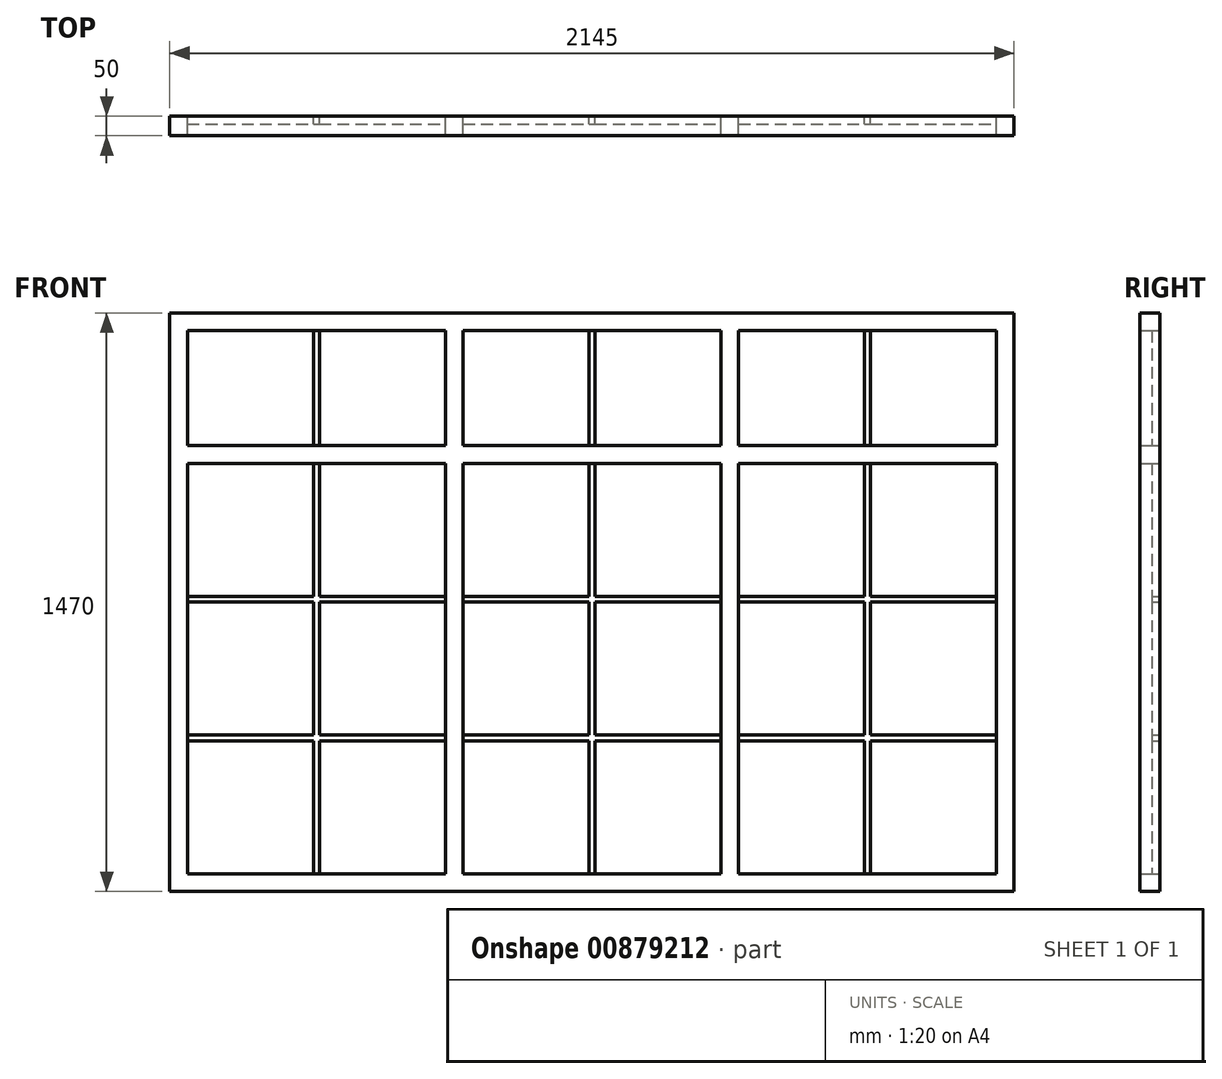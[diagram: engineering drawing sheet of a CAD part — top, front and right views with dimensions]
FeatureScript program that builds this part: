
annotation { "Feature Type Name" : "Feature", "Feature Type Description" : "" }
export const myFeature = defineFeature(function(context is Context, id is Id, definition is map)
    precondition{}
    {
        {
            var Q0;
            Q0=qCreatedBy(makeId("Front.planeOp"),FACE);
            var sketch = newSketch(context, id + "F0", { "sketchPlane" : qUnion([Q0])});
            skLineSegment(sketch, "E0.bottom", {"start": v(0, 0) * mm, "end": v(2145, 0) * mm});
            skLineSegment(sketch, "E0.top", {"start": v(0, 1470) * mm, "end": v(2145, 1470) * mm});
            skLineSegment(sketch, "E0.left", {"start": v(0, 0) * mm, "end": v(0, 1470) * mm});
            skLineSegment(sketch, "E0.right", {"start": v(2145, 0) * mm, "end": v(2145, 1470) * mm});
            skLineSegment(sketch, "E1.bottom", {"start": v(45, 1425) * mm, "end": v(700, 1425) * mm});
            skLineSegment(sketch, "E1.top", {"start": v(45, 45) * mm, "end": v(700, 45) * mm});
            skLineSegment(sketch, "E1.left", {"start": v(45, 1425) * mm, "end": v(45, 1132.5) * mm});
            skLineSegment(sketch, "E1.right", {"start": v(700, 1425) * mm, "end": v(700, 1132.5) * mm});
            skLineSegment(sketch, "E2.bottom", {"start": v(745, 1425) * mm, "end": v(1400, 1425) * mm});
            skLineSegment(sketch, "E2.top", {"start": v(745, 1132.5) * mm, "end": v(1400, 1132.5) * mm});
            skLineSegment(sketch, "E2.left", {"start": v(745, 1425) * mm, "end": v(745, 1132.5) * mm});
            skLineSegment(sketch, "E2.right", {"start": v(1400, 1425) * mm, "end": v(1400, 1132.5) * mm});
            skLineSegment(sketch, "E3.bottom", {"start": v(745, 1087.5) * mm, "end": v(1400, 1087.5) * mm});
            skLineSegment(sketch, "E3.top", {"start": v(745, 45) * mm, "end": v(1400, 45) * mm});
            skLineSegment(sketch, "E3.left", {"start": v(745, 1087.5) * mm, "end": v(745, 45) * mm});
            skLineSegment(sketch, "E3.right", {"start": v(1400, 1087.5) * mm, "end": v(1400, 45) * mm});
            skLineSegment(sketch, "E4.bottom", {"start": v(1445, 1425) * mm, "end": v(2100, 1425) * mm});
            skLineSegment(sketch, "E4.top", {"start": v(1445, 45) * mm, "end": v(2100, 45) * mm});
            skLineSegment(sketch, "E4.left", {"start": v(1445, 1425) * mm, "end": v(1445, 1132.5) * mm});
            skLineSegment(sketch, "E4.right", {"start": v(2100, 1425) * mm, "end": v(2100, 1132.5) * mm});
            skLineSegment(sketch, "E5.bottom", {"start": v(45, 1132.5) * mm, "end": v(700, 1132.5) * mm});
            skLineSegment(sketch, "E5.top", {"start": v(45, 1087.5) * mm, "end": v(700, 1087.5) * mm});
            skLineSegment(sketch, "E6.trimOffspring", {"start": v(45, 1087.5) * mm, "end": v(45, 45) * mm});
            skLineSegment(sketch, "E7.trimOffspring", {"start": v(700, 1087.5) * mm, "end": v(700, 45) * mm});
            skLineSegment(sketch, "E8.bottom", {"start": v(1445, 1132.5) * mm, "end": v(2100, 1132.5) * mm});
            skLineSegment(sketch, "E8.top", {"start": v(1445, 1087.5) * mm, "end": v(2100, 1087.5) * mm});
            skLineSegment(sketch, "E9.trimOffspring", {"start": v(1445, 1087.5) * mm, "end": v(1445, 45) * mm});
            skLineSegment(sketch, "E10.trimOffspring", {"start": v(2100, 1087.5) * mm, "end": v(2100, 45) * mm});
            skSolve(sketch);
        }
        {
            var Q0;
            Q0=qSketchRegion(id+"F0",true);
            extrude(context, id + "F1", {"entities" : qUnion([Q0]), "depth" : 50 * mm, "offsetDistance" : 25 * mm});
        }
        {
            var Q0;
            Q0=qCreatedBy(makeId("Front.planeOp"),FACE);
            var sketch = newSketch(context, id + "F2", { "sketchPlane" : qUnion([Q0])});
            skLineSegment(sketch, "E11.bottom", {"start": v(45, 750) * mm, "end": v(365, 750) * mm});
            skLineSegment(sketch, "E11.top", {"start": v(45, 735) * mm, "end": v(365, 735) * mm});
            skLineSegment(sketch, "E11.left", {"start": v(45, 750) * mm, "end": v(45, 735) * mm});
            skLineSegment(sketch, "E11.right", {"start": v(700, 750) * mm, "end": v(700, 735) * mm});
            skLineSegment(sketch, "E12.bottom", {"start": v(45, 397.5) * mm, "end": v(365, 397.5) * mm});
            skLineSegment(sketch, "E12.top", {"start": v(45, 382.5) * mm, "end": v(365, 382.5) * mm});
            skLineSegment(sketch, "E12.left", {"start": v(45, 397.5) * mm, "end": v(45, 382.5) * mm});
            skLineSegment(sketch, "E12.right", {"start": v(700, 397.5) * mm, "end": v(700, 382.5) * mm});
            skLineSegment(sketch, "E13.bottom", {"start": v(365, 1087.5) * mm, "end": v(380, 1087.5) * mm});
            skLineSegment(sketch, "E13.top", {"start": v(365, 45) * mm, "end": v(380, 45) * mm});
            skLineSegment(sketch, "E13.left", {"start": v(365, 1087.5) * mm, "end": v(365, 750) * mm});
            skLineSegment(sketch, "E13.right", {"start": v(380, 1087.5) * mm, "end": v(380, 750) * mm});
            skLineSegment(sketch, "E14.bottom", {"start": v(365, 1425) * mm, "end": v(380, 1425) * mm});
            skLineSegment(sketch, "E14.top", {"start": v(365, 1132.5) * mm, "end": v(380, 1132.5) * mm});
            skLineSegment(sketch, "E14.left", {"start": v(365, 1425) * mm, "end": v(365, 1132.5) * mm});
            skLineSegment(sketch, "E14.right", {"start": v(380, 1425) * mm, "end": v(380, 1132.5) * mm});
            skLineSegment(sketch, "E15.bottom", {"start": v(1065, 1425) * mm, "end": v(1080, 1425) * mm});
            skLineSegment(sketch, "E15.top", {"start": v(1065, 1132.5) * mm, "end": v(1080, 1132.5) * mm});
            skLineSegment(sketch, "E15.left", {"start": v(1065, 1425) * mm, "end": v(1065, 1132.5) * mm});
            skLineSegment(sketch, "E15.right", {"start": v(1080, 1425) * mm, "end": v(1080, 1132.5) * mm});
            skLineSegment(sketch, "E16.bottom", {"start": v(745, 750) * mm, "end": v(1065, 750) * mm});
            skLineSegment(sketch, "E16.top", {"start": v(745, 735) * mm, "end": v(1065, 735) * mm});
            skLineSegment(sketch, "E16.left", {"start": v(745, 750) * mm, "end": v(745, 735) * mm});
            skLineSegment(sketch, "E16.right", {"start": v(1400, 750) * mm, "end": v(1400, 735) * mm});
            skLineSegment(sketch, "E17.bottom", {"start": v(745, 397.5) * mm, "end": v(1065, 397.5) * mm});
            skLineSegment(sketch, "E17.top", {"start": v(745, 382.5) * mm, "end": v(1065, 382.5) * mm});
            skLineSegment(sketch, "E17.left", {"start": v(745, 397.5) * mm, "end": v(745, 382.5) * mm});
            skLineSegment(sketch, "E17.right", {"start": v(1400, 397.5) * mm, "end": v(1400, 382.5) * mm});
            skLineSegment(sketch, "E18.bottom", {"start": v(1065, 1087.5) * mm, "end": v(1080, 1087.5) * mm});
            skLineSegment(sketch, "E18.top", {"start": v(1065, 45) * mm, "end": v(1080, 45) * mm});
            skLineSegment(sketch, "E18.left", {"start": v(1065, 1087.5) * mm, "end": v(1065, 750) * mm});
            skLineSegment(sketch, "E18.right", {"start": v(1080, 1087.5) * mm, "end": v(1080, 750) * mm});
            skLineSegment(sketch, "E19.bottom", {"start": v(1765, 1425) * mm, "end": v(1780, 1425) * mm});
            skLineSegment(sketch, "E19.top", {"start": v(1765, 1132.5) * mm, "end": v(1780, 1132.5) * mm});
            skLineSegment(sketch, "E19.left", {"start": v(1780, 1425) * mm, "end": v(1780, 1132.5) * mm});
            skLineSegment(sketch, "E19.right", {"start": v(1765, 1425) * mm, "end": v(1765, 1132.5) * mm});
            skLineSegment(sketch, "E20.bottom", {"start": v(1765, 1087.5) * mm, "end": v(1780, 1087.5) * mm});
            skLineSegment(sketch, "E20.top", {"start": v(1765, 45) * mm, "end": v(1780, 45) * mm});
            skLineSegment(sketch, "E20.left", {"start": v(1765, 1087.5) * mm, "end": v(1765, 750) * mm});
            skLineSegment(sketch, "E20.right", {"start": v(1780, 1087.5) * mm, "end": v(1780, 750) * mm});
            skLineSegment(sketch, "E21.bottom", {"start": v(1445, 735) * mm, "end": v(1765, 735) * mm});
            skLineSegment(sketch, "E21.top", {"start": v(1445, 750) * mm, "end": v(1765, 750) * mm});
            skLineSegment(sketch, "E21.left", {"start": v(1445, 750) * mm, "end": v(1445, 735) * mm});
            skLineSegment(sketch, "E21.right", {"start": v(2100, 750) * mm, "end": v(2100, 735) * mm});
            skLineSegment(sketch, "E22.bottom", {"start": v(1445, 397.5) * mm, "end": v(1765, 397.5) * mm});
            skLineSegment(sketch, "E22.top", {"start": v(1445, 382.5) * mm, "end": v(1765, 382.5) * mm});
            skLineSegment(sketch, "E22.left", {"start": v(1445, 397.5) * mm, "end": v(1445, 382.5) * mm});
            skLineSegment(sketch, "E22.right", {"start": v(2100, 397.5) * mm, "end": v(2100, 382.5) * mm});
            skLineSegment(sketch, "E23.trimOffspring", {"start": v(380, 750) * mm, "end": v(700, 750) * mm});
            skLineSegment(sketch, "E24.trimOffspring", {"start": v(365, 735) * mm, "end": v(365, 397.5) * mm});
            skLineSegment(sketch, "E25.trimOffspring", {"start": v(380, 735) * mm, "end": v(700, 735) * mm});
            skLineSegment(sketch, "E26.trimOffspring", {"start": v(380, 735) * mm, "end": v(380, 397.5) * mm});
            skLineSegment(sketch, "E27.trimOffspring", {"start": v(380, 397.5) * mm, "end": v(700, 397.5) * mm});
            skLineSegment(sketch, "E28.trimOffspring", {"start": v(365, 382.5) * mm, "end": v(365, 45) * mm});
            skLineSegment(sketch, "E29.trimOffspring", {"start": v(380, 382.5) * mm, "end": v(700, 382.5) * mm});
            skLineSegment(sketch, "E30.trimOffspring", {"start": v(380, 382.5) * mm, "end": v(380, 45) * mm});
            skLineSegment(sketch, "E31.trimOffspring", {"start": v(1080, 750) * mm, "end": v(1400, 750) * mm});
            skLineSegment(sketch, "E32.trimOffspring", {"start": v(1065, 735) * mm, "end": v(1065, 397.5) * mm});
            skLineSegment(sketch, "E33.trimOffspring", {"start": v(1080, 735) * mm, "end": v(1400, 735) * mm});
            skLineSegment(sketch, "E34.trimOffspring", {"start": v(1080, 735) * mm, "end": v(1080, 397.5) * mm});
            skLineSegment(sketch, "E35.trimOffspring", {"start": v(1765, 735) * mm, "end": v(1765, 397.5) * mm});
            skLineSegment(sketch, "E36.trimOffspring", {"start": v(1780, 750) * mm, "end": v(2100, 750) * mm});
            skLineSegment(sketch, "E37.trimOffspring", {"start": v(1780, 735) * mm, "end": v(1780, 397.5) * mm});
            skLineSegment(sketch, "E38.trimOffspring", {"start": v(1780, 735) * mm, "end": v(2100, 735) * mm});
            skLineSegment(sketch, "E39.trimOffspring", {"start": v(1065, 382.5) * mm, "end": v(1065, 45) * mm});
            skLineSegment(sketch, "E40.trimOffspring", {"start": v(1080, 397.5) * mm, "end": v(1400, 397.5) * mm});
            skLineSegment(sketch, "E41.trimOffspring", {"start": v(1080, 382.5) * mm, "end": v(1080, 45) * mm});
            skLineSegment(sketch, "E42.trimOffspring", {"start": v(1080, 382.5) * mm, "end": v(1400, 382.5) * mm});
            skLineSegment(sketch, "E43.trimOffspring", {"start": v(1765, 382.5) * mm, "end": v(1765, 45) * mm});
            skLineSegment(sketch, "E44.trimOffspring", {"start": v(1780, 382.5) * mm, "end": v(1780, 45) * mm});
            skLineSegment(sketch, "E45.trimOffspring", {"start": v(1780, 397.5) * mm, "end": v(2100, 397.5) * mm});
            skLineSegment(sketch, "E46.trimOffspring", {"start": v(1780, 382.5) * mm, "end": v(2100, 382.5) * mm});
            skSolve(sketch);
        }
        {
            var Q0;
            Q0=qSketchRegion(id+"F2",true);
            extrude(context, id + "F3", {"entities" : qUnion([Q0]), "operationType" : NewBodyOperationType.ADD, "depth" : 20 * mm, "offsetDistance" : 25 * mm});
        }
    });
